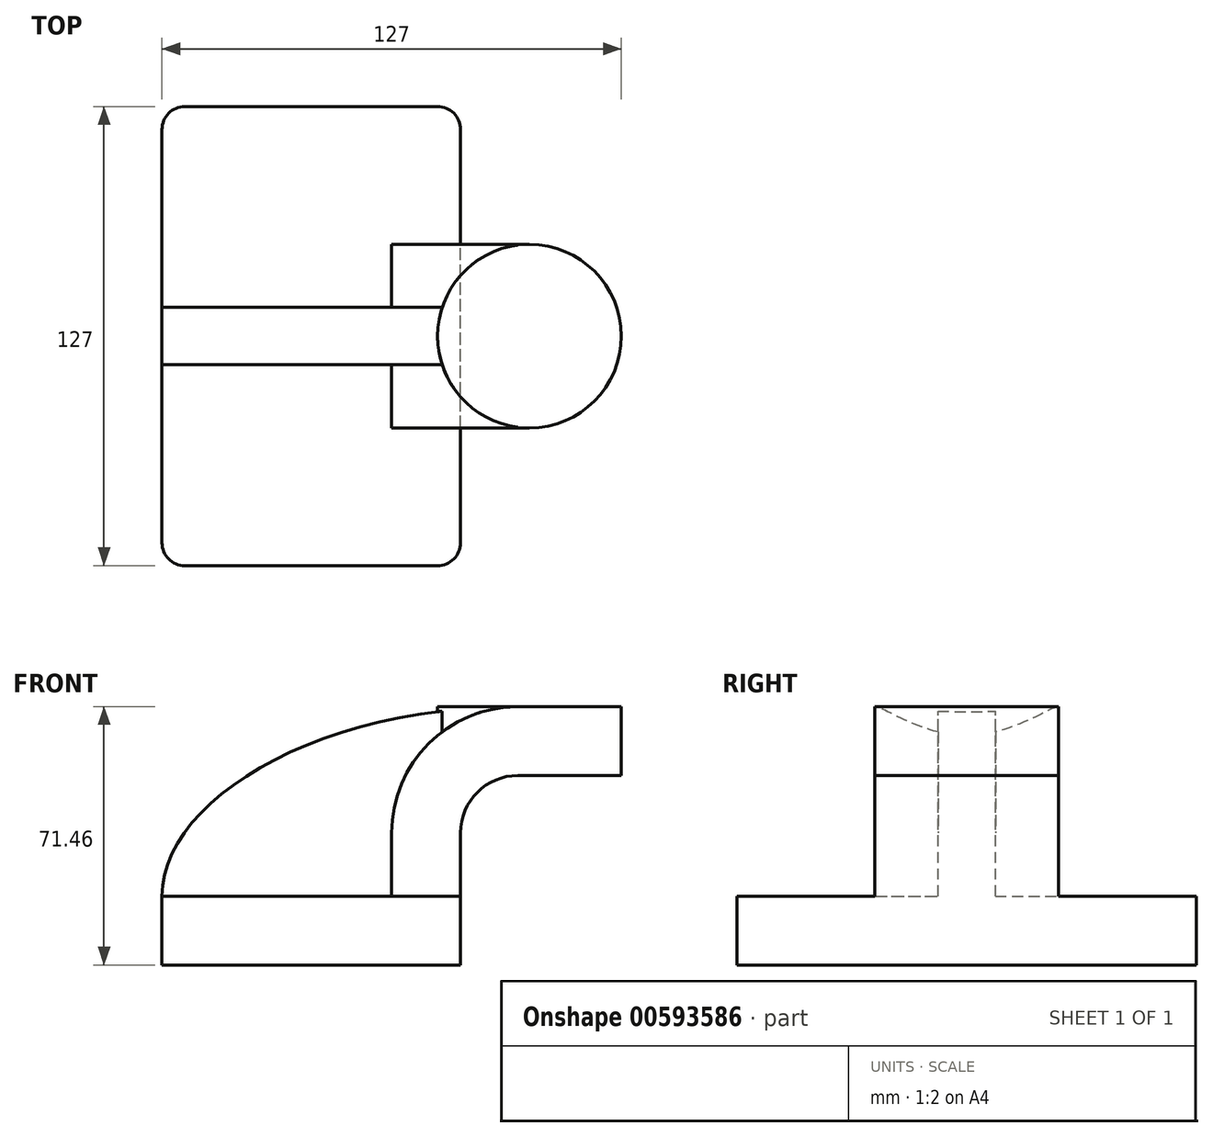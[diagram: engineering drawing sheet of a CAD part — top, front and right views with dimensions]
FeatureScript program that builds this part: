
annotation { "Feature Type Name" : "Feature", "Feature Type Description" : "" }
export const myFeature = defineFeature(function(context is Context, id is Id, definition is map)
    precondition{}
    {
        {
            var Q0;
            Q0=qCreatedBy(makeId("Front.planeOp"),FACE);
            var sketch = newSketch(context, id + "F0", { "sketchPlane" : qUnion([Q0])});
            skLineSegment(sketch, "E0.bottom", {"start": v(-41.28, -9.53) * mm, "end": v(41.28, -9.53) * mm});
            skLineSegment(sketch, "E0.top", {"start": v(-41.28, 9.53) * mm, "end": v(41.28, 9.53) * mm});
            skLineSegment(sketch, "E0.left", {"start": v(-41.28, -9.53) * mm, "end": v(-41.28, 9.53) * mm});
            skLineSegment(sketch, "E0.right", {"start": v(41.28, -9.53) * mm, "end": v(41.28, 9.53) * mm});
            skPoint(sketch, "E0.middle", {"position": v(0, 0) * mm});
            skLineSegment(sketch, "E1.bottom", {"start": v(60.32, 66.67) * mm, "end": v(111.12, 66.67) * mm});
            skLineSegment(sketch, "E1.top", {"start": v(60.32, 38.1) * mm, "end": v(111.13, 38.1) * mm});
            skLineSegment(sketch, "E1.left", {"start": v(60.32, 66.67) * mm, "end": v(60.32, 38.1) * mm});
            skLineSegment(sketch, "E1.right", {"start": v(111.12, 66.67) * mm, "end": v(111.12, 38.1) * mm});
            skLineSegment(sketch, "E2", {"start": v(41.28, 9.52) * mm, "end": v(41.28, 27) * mm});
            skArc(sketch, "E3", {"start": v(57.15, 42.88) * mm, "mid": v(45.92, 38.23) * mm, "end": v(41.27, 27) * mm});
            skLineSegment(sketch, "E4", {"start": v(57.15, 42.88) * mm, "end": v(85.72, 42.88) * mm});
            skPoint(sketch, "E4.endSnap0", {"position": v(85.72, 38.1) * mm});
            skLineSegment(sketch, "E5.0", {"start": v(57.15, 61.93) * mm, "end": v(85.72, 61.93) * mm});
            skArc(sketch, "E5.1", {"start": v(57.15, 61.93) * mm, "mid": v(32.45, 51.7) * mm, "end": v(22.22, 27) * mm});
            skLineSegment(sketch, "E5.2", {"start": v(22.22, 9.52) * mm, "end": v(22.22, 27) * mm});
            skLineSegment(sketch, "E6", {"start": v(85.72, 38.1) * mm, "end": v(85.72, 66.67) * mm});
            skFitSpline(sketch, "E7", {"points": [v(-41.28, 9.53) * mm, v(57.15, 61.93) * mm], "startDerivative": vector(0, 77.31) * mm, "endDerivative": vector(171.45, 0) * mm});
            skPoint(sketch, "E8", {"position": v(71.44, 61.93) * mm});
            skSolve(sketch);
        }
        {
            var Q0;
            Q0=makeQuery(id+"F0.imprint","IMPRINT",FACE,{"disambiguationData":[TD([[makeQuery(id+"F0.imprint","IMPRINT",EDGE,{"derivedFrom":sQuery(id+"F0.wireOp",EDGE,"E0.bottom")}),1.0]])]});
            extrude(context, id + "F1", {"entities" : qUnion([Q0]), "endBound" : BoundingType.SYMMETRIC, "depth" : 127 * mm, "offsetDistance" : 25.4 * mm});
        }
        {
            var Q0;
            {var subQ1=sQuery(id+"F0.wireOp",EDGE,"E2");Q0=makeQuery(id+"F0.imprint","IMPRINT",FACE,{"disambiguationData":[TD([[makeQuery(id+"F0.imprint","IMPRINT",EDGE,{"derivedFrom":subQ1}),1.0]])]});}
            extrude(context, id + "F2", {"entities" : qUnion([Q0]), "operationType" : NewBodyOperationType.ADD, "endBound" : BoundingType.SYMMETRIC, "depth" : 50.8 * mm, "offsetDistance" : 25.4 * mm});
        }
        {
            var Q0;
            Q0=makeQuery(id+"F0.imprint","IMPRINT",FACE,{"disambiguationData":[TD([[makeQuery(id+"F0.imprint","IMPRINT",EDGE,{"derivedFrom":sQuery(id+"F0.wireOp",EDGE,"E5.1")}),-1.0]])]});
            extrude(context, id + "F3", {"entities" : qUnion([Q0]), "operationType" : NewBodyOperationType.ADD, "endBound" : BoundingType.SYMMETRIC, "depth" : 15.88 * mm, "offsetDistance" : 25.4 * mm});
        }
        {
            var Q0;
            {var subQ0=sQuery(id+"F0.wireOp",EDGE,"E5.0");var subQ1=sQuery(id+"F0.wireOp",EDGE,"E1.left");var subQ2=makeQuery(id+"F0.imprint","INTERSECT",VERTEX,{"derivedFrom":[subQ1,subQ0]});Q0=makeQuery(id+"F0.imprint","IMPRINT",FACE,{"disambiguationData":[TD([[makeQuery(id+"F0.imprint","IMPRINT",EDGE,{"disambiguationData":[TD([[subQ2,-1.0]])],"derivedFrom":subQ1}),1.0]])]});}
            var Q1;
            Q1=sQuery(id+"F0.wireOp",EDGE,"E1.left");
            revolve(context, id + "F4", {"operationType" : NewBodyOperationType.ADD, "entities" : qUnion([Q0]), "axis" : qUnion([Q1]), "revolveType" : RevolveType.FULL});
        }
        {
            var Q0;
            Q0=makeQuery(id+"F1.opExtrude","CAP_EDGE",EDGE,{"disambiguationData":[OSD([sQuery(id+"F0.wireOp",EDGE,"E0.left")])],"isStart":false});
            var Q1;
            Q1=makeQuery(id+"F1.opExtrude","CAP_EDGE",EDGE,{"disambiguationData":[OSD([sQuery(id+"F0.wireOp",EDGE,"E0.right")])],"isStart":false});
            var Q2;
            Q2=makeQuery(id+"F1.opExtrude","CAP_EDGE",EDGE,{"disambiguationData":[OSD([sQuery(id+"F0.wireOp",EDGE,"E0.right")])],"isStart":true});
            var Q3;
            Q3=makeQuery(id+"F1.opExtrude","CAP_EDGE",EDGE,{"disambiguationData":[OSD([sQuery(id+"F0.wireOp",EDGE,"E0.left")])],"isStart":true});
            fillet(context, id + "F5", {"entities" : qUnion([Q0, Q1, Q2, Q3]), "radius" : 6.35 * mm, "tangentPropagation" : true, "allowEdgeOverflow" : false});
        }
    });
